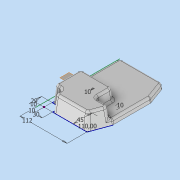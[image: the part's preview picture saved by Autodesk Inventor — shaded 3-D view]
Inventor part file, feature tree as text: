
AUTODESK INVENTOR PART (.ipt)
format: ipt  version: 2022 (Build 260153070, 153G)  size: 2,284,032 bytes
history: native  units: mm
features: other x7, sketch x6, plane x2, extrude x2, fillet x2
ambient origin geometry x8: Origin, YZ Plane, XZ Plane, XY Plane, X Axis, Y Axis, Z Axis, Center Point
bodies: Body1 (feature_tree), Body2 (feature_tree)
feature tree (19):
  other  "P00173-09-018.ipt"
  other  "Blocks"
  sketch  "Sketch8"  dims[d7=15.0mm]
  plane  "Work Plane1"
  plane  "Work Plane2"
  sketch  "Sketch12"  dims[d10=8.0mm]
  sketch  "Sketch13"  dims[d11=30.0mm d12=29.0mm d13=19.198622mm d14=45.0mm d15=112.0mm d21=19.198622mm d22=12.0mm d23=-0.872665mm d24=5.0mm d25=10.0mm d26=19.198622mm]
  extrude  "Extrusion1"  Depth=15.0mm
  extrude  "Extrusion3"  Depth=10.0mm
  fillet  "Fillet1"  Radius=10.0mm
  fillet  "Fillet3"  Radius=10.0mm
  other  "TaggingFeature2"
  sketch  "Sketch9"  dims[d8=38.0mm d9=-0.872665mm]
  other  "Side"
  sketch  "Sketch3"  dims[d1=10.0mm d2=15.0mm]
  sketch  "Sketch6"  dims[d3=10.0mm d4=10.0mm d5=10.0mm d6=10.0mm]
  other  "Bottom"
  other  "Solid6::P00173-09-018.ipt"
  other  "Srf2"
